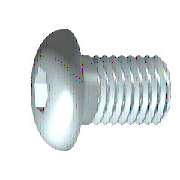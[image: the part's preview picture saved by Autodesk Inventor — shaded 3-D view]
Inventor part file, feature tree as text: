
AUTODESK INVENTOR PART (.ipt)
format: ipt  version: 2022 (Build 260153000, 153)  size: 192,512 bytes
history: native  units: mm (DEFAULTED — no unit token found)
features: sketch x2, extrude x1, plane x1, fillet x1
ambient origin geometry x7: Origin, YZ Plane, XY Plane, X Axis, Y Axis, Z Axis, Center Point
bodies: Solid1 (feature_tree), Body (feature_tree)
feature tree (5):
  extrude  "Slot"  Depth=3.3mm
  plane  "Work Plane1"
  fillet  "Fillet2"  Radius=3.3mm
  sketch  "Sketch1"  dims[d1=27.0mm d2=0.61355mm d3=3.3mm]
  sketch  "Sketch2"  dims[d4=2.08mm d5=60.0deg d6=6.0mm d7=6.0mm d8=4.618802mm d9=10.5mm d10=90.0deg d11=10.0mm d12=0.0mm d13=27.0mm d14=0.0mm d15=0.61345mm d16=0.61345mm d17=2.56mm d19=0.0mm d26=30.0mm d27=45.0deg d28=0.0mm d29=0.0mm d30=0.5mm]
